# Revit family: 950_ROUTER
name_source: partatom
category: Specialty Equipment
units: mm (PartAtom-declared; Revit-internal decimal feet)

## family parameters
Always vertical = No
Cut with Voids When Loaded = No
Part Type = Normal
Room Calculation Point = No
Round Connector Dimension = Use Diameter
Shared = No
Work Plane-Based = No

## types (1)
- 950_ROUTER
    950 = 240V version
    950-110V = 110V version
    Ambient temperature = 0 °C to +40 °C
    Colour = Body: White (RAL 9003)
Lid: Translucent red (RAL 3027)
    DALI cable = 0.5 mm² – 2.5 mm²
Max. length: 300 m @ 1.5 mm²
    DALI data transfer = DALI-2 Application Controller (Multi Master)
IEC62386 Part 101, 103
See DALI Alliance Website for full detail of
supported parts https://www.dali-alliance.
org/products
    DALI-OUT current = 4 × 240 mA (guaranteed)
4 x 250mA (maximum)
    Default Elevation = 0 mm  [stored 0 ft]
    Designer = 5.7.0 or later
    Developed by = Prompt Engineering Consultancy Services
    Developer Website = https://promptconsult.com
    Diameter = 32 mm  [stored 0.104987 ft]
    Dimensions = 10U –177 mm x 99.5 mm x 58 mm
    EMC emission = EN 61000-6-3, EN 55015
    EMC immunity = EN 55024, EN 61547
    Environment = Complies with WEEE and RoHS directives
    Ethernet = 2 × RJ45 10/100/1000 Mb/s, Cat 5E up to 100 m
(Auto MDI/MDI-X crossover)
Sys for Lighting System Network
Aux for developer purposes only
    Height = 250 mm  [stored 0.82021 ft]
    IP rating = IP20 (IP00 at connectors)
    LCD = Colour display 320x240px
    Mains cable = Solid core up to 2.5 mm²
Stranded up to 2.5 mm²
Stranded up to 2.5 mm²
    Mains supply = 240 V: 220 VAC – 240 VAC (nominal)
198 VAC – 264 VAC (absolute)
45 Hz – 65 Hz
110V: 100 VAC – 120 VAC (nominal)
90 VAC – 140 VAC (absolute)
45 Hz – 65 Hz
    Manufacturer = Helvar
    Manufacturer Contry = Finland
    Manufacturer Website = https://helvar.com
    Material = Body: Polycarbonate
Lid: Polycarbonate
    Mounting = DIN Rail. Keep the Ethernet cable separate
from all mains and DALI wirings
    Power circuit protection = Internal fuse. External protection according
to supply wiring, max. 6 A.
    Power consumption = 35 W (All DALI subnets fully loaded)
    Power factor = > 0.95 at full load
    Relative humidity = Max. 90 %, noncondensing
    Router Height = 100 mm  [stored 0.328084 ft]
    Safety = EN 61347
    Sensor Body Height = 21 mm  [stored 0.0688976 ft]
    Storage temperature = –10 °C to +70 °C
    Support Hanger Angle = 45.00°
    Support Height = 35 mm  [stored 0.114829 ft]
    Support Width = 10 mm  [stored 0.0328084 ft]
    Weight = 460 g
    Width = 177 mm  [stored 0.580709 ft]

note: [stored X ft] marks values corroborated as IEEE doubles in the binary element streams (Revit-internal decimal feet)

## geometry (parser evidence)
native form markers: Sweep x2
no freeform markers — native parametric forms only
